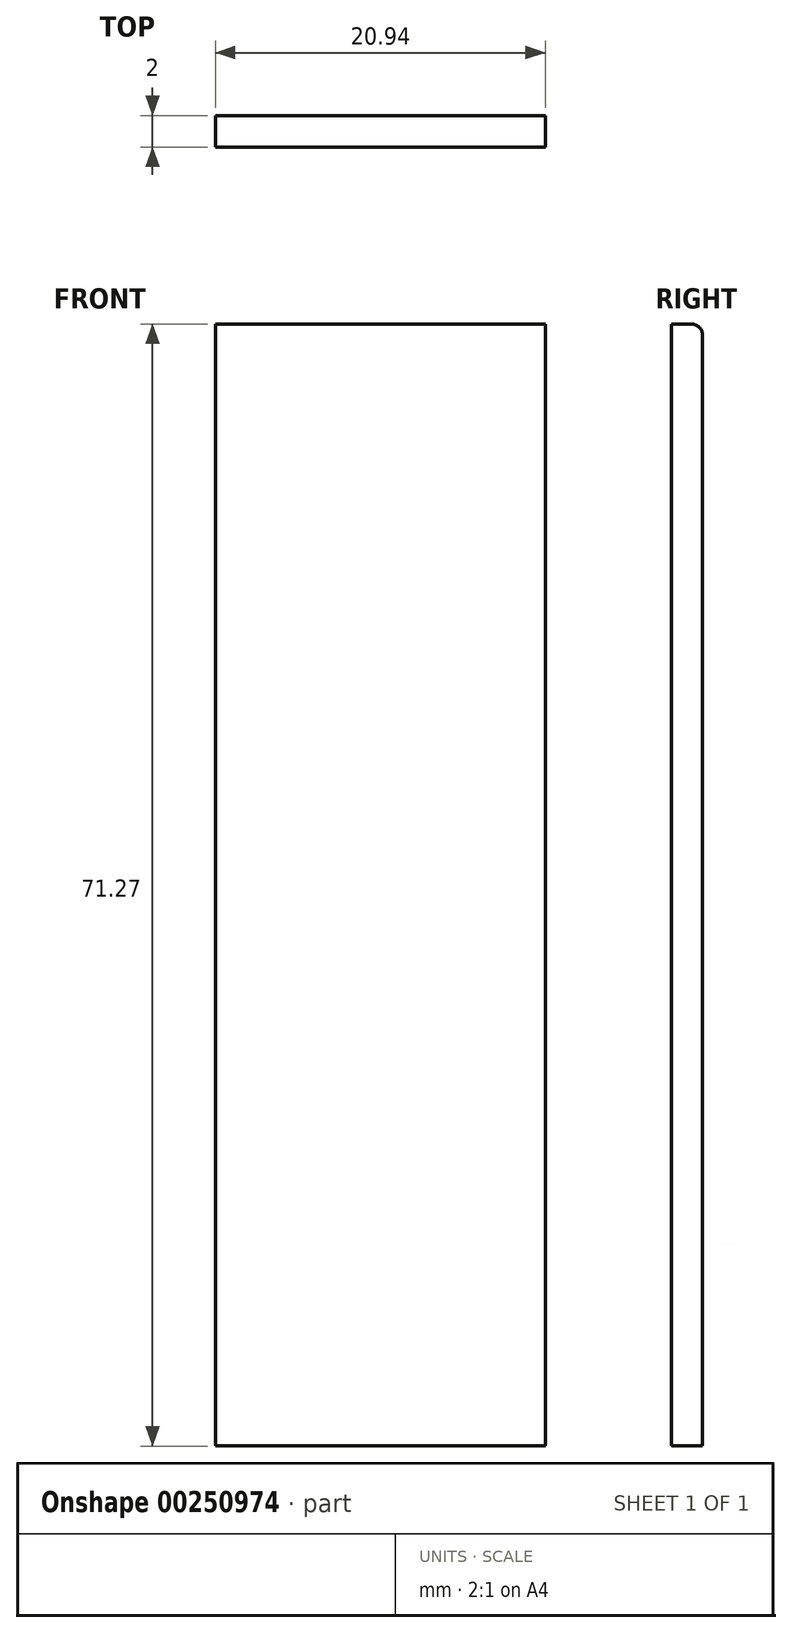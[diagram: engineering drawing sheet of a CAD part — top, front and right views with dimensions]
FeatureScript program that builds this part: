
annotation { "Feature Type Name" : "Feature", "Feature Type Description" : "" }
export const myFeature = defineFeature(function(context is Context, id is Id, definition is map)
    precondition{}
    {
        {
            var Q0;
            Q0=qCreatedBy(makeId("Front.planeOp"),FACE);
            var sketch = newSketch(context, id + "F0", { "sketchPlane" : qUnion([Q0])});
            skLineSegment(sketch, "E0.bottom", {"start": v(-11.19, 31.7) * mm, "end": v(9.75, 31.7) * mm});
            skLineSegment(sketch, "E0.top", {"start": v(-11.19, -39.57) * mm, "end": v(9.75, -39.57) * mm});
            skLineSegment(sketch, "E0.left", {"start": v(-11.19, 31.7) * mm, "end": v(-11.19, -39.57) * mm});
            skLineSegment(sketch, "E0.right", {"start": v(9.75, 31.7) * mm, "end": v(9.75, -39.57) * mm});
            skSolve(sketch);
        }
        {
            var Q0;
            Q0 = qSketchRegion(id + "F0", true);
            extrude(context, id + "F1", {"entities" : qUnion([Q0]), "depth" : 2 * mm});
        }
        {
            var Q0;
            Q0=makeQuery(id+"F1.opExtrude","CAP_EDGE",EDGE,{"disambiguationData":[OSD([sQuery(id+"F0.wireOp",EDGE,"E0.bottom")])],"isStart":true});
            fillet(context, id + "F2", {"entities" : qUnion([Q0]), "radius" : 0.72 * mm, "tangentPropagation" : true, "allowEdgeOverflow" : false});
        }
    });
